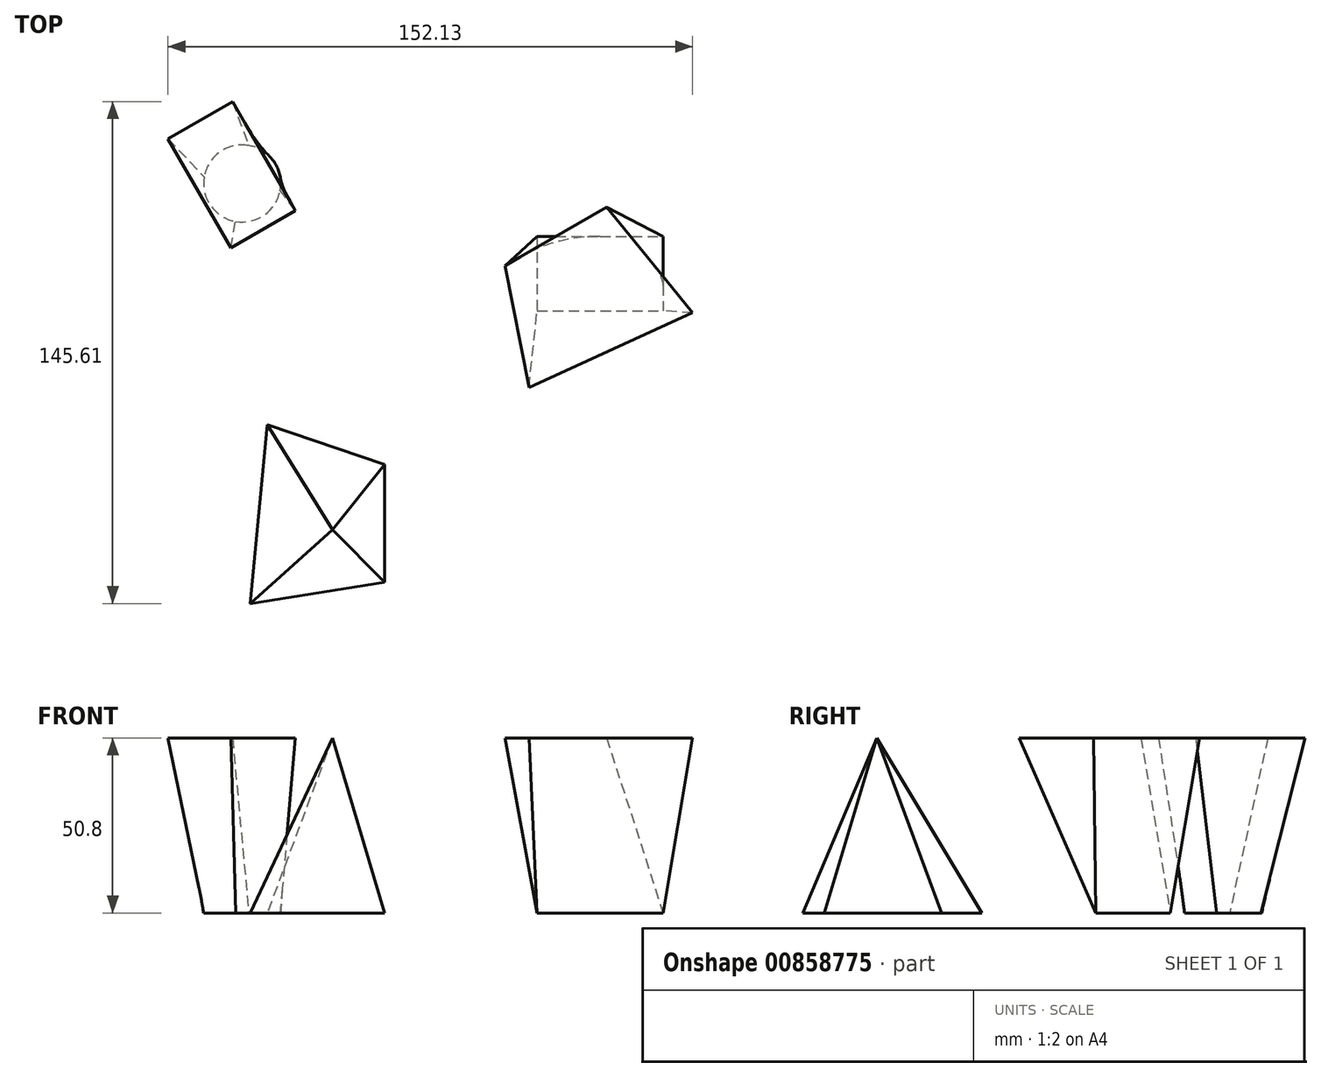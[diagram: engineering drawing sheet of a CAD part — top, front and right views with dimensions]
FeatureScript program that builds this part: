
annotation { "Feature Type Name" : "Feature", "Feature Type Description" : "" }
export const myFeature = defineFeature(function(context is Context, id is Id, definition is map)
    precondition{}
    {
        {
            var Q0;
            Q0=qCreatedBy(makeId("Top.planeOp"),FACE);
            var sketch = newSketch(context, id + "F0", { "sketchPlane" : qUnion([Q0])});
            skCircle(sketch, "E0", {"center": v(-62.28, 52.52) * mm, "radius": 11.18 * mm});
            skLineSegment(sketch, "E1.bottom", {"start": v(23.25, 37.16) * mm, "end": v(59.79, 37.16) * mm});
            skLineSegment(sketch, "E1.top", {"start": v(23.25, 15.57) * mm, "end": v(59.79, 15.57) * mm});
            skLineSegment(sketch, "E1.left", {"start": v(23.25, 37.16) * mm, "end": v(23.25, 15.57) * mm});
            skLineSegment(sketch, "E1.right", {"start": v(59.79, 37.16) * mm, "end": v(59.79, 15.57) * mm});
            skLineSegment(sketch, "E2", {"start": v(-55, -17.45) * mm, "end": v(-20.95, -29.08) * mm});
            skLineSegment(sketch, "E3", {"start": v(-20.95, -29.08) * mm, "end": v(-20.95, -63.13) * mm});
            skLineSegment(sketch, "E4", {"start": v(-20.95, -63.13) * mm, "end": v(-59.98, -69.35) * mm});
            skLineSegment(sketch, "E5", {"start": v(-59.98, -69.35) * mm, "end": v(-55, -17.45) * mm});
            skLineSegment(sketch, "E6", {"start": v(-82.91, 71.7) * mm, "end": v(-82.91, 30.26) * mm, "construction": true});
            skSolve(sketch);
        }
        {
            var Q0;
            Q0=qCreatedBy(makeId("Top.planeOp"),FACE);
            cPlane(context, id + "F1", {"entities" : qUnion([Q0]), "cplaneType" : CPlaneType.OFFSET, "offset" : 50.8 * mm, "width" : 152.4 * mm, "height" : 152.4 * mm});
        }
        {
            var Q0;
            Q0=qCreatedBy(id+"F1.planeOp",FACE);
            var sketch = newSketch(context, id + "F2", { "sketchPlane" : qUnion([Q0])});
            skCircle(sketch, "E7.0", {"center": v(-36.07, -47.94) * mm, "radius": 11.18 * mm});
            skLineSegment(sketch, "E7.1.0", {"start": v(-65.53, 33.82) * mm, "end": v(-46.83, 44.61) * mm});
            skLineSegment(sketch, "E7.1.1", {"start": v(-46.83, 44.61) * mm, "end": v(-65.1, 76.26) * mm});
            skLineSegment(sketch, "E7.1.2", {"start": v(-65.1, 76.26) * mm, "end": v(-83.8, 65.46) * mm});
            skLineSegment(sketch, "E7.1.3", {"start": v(-83.8, 65.46) * mm, "end": v(-65.53, 33.82) * mm});
            skLineSegment(sketch, "E7.2.0", {"start": v(20.9, -6.64) * mm, "end": v(68.33, 15) * mm});
            skLineSegment(sketch, "E7.2.1", {"start": v(68.33, 15) * mm, "end": v(43.42, 45.68) * mm});
            skLineSegment(sketch, "E7.2.2", {"start": v(43.42, 45.68) * mm, "end": v(13.94, 28.66) * mm});
            skLineSegment(sketch, "E7.2.3", {"start": v(13.94, 28.66) * mm, "end": v(20.9, -6.64) * mm});
            skSolve(sketch);
        }
        {
            var Q0;
            Q0=makeQuery(id+"F2.imprint","IMPRINT",FACE,{"disambiguationData":[TD([[makeQuery(id+"F2.imprint","IMPRINT",EDGE,{"derivedFrom":sQuery(id+"F2.wireOp",EDGE,"E7.2.0")}),1.0]])]});
            var Q1;
            Q1=makeQuery(id+"F0.imprint","IMPRINT",FACE,{"disambiguationData":[TD([[makeQuery(id+"F0.imprint","IMPRINT",EDGE,{"derivedFrom":sQuery(id+"F0.wireOp",EDGE,"E1.bottom")}),-1.0]])]});
            loft(context, id + "F3", {"sheetProfilesArray" : [{ "sheetProfileEntities" : qUnion([Q0]) }, { "sheetProfileEntities" : qUnion([Q1]) }]});
        }
        {
            var Q0;
            Q0=makeQuery(id+"F2.imprint","IMPRINT",FACE,{"disambiguationData":[TD([[makeQuery(id+"F2.imprint","IMPRINT",EDGE,{"derivedFrom":sQuery(id+"F2.wireOp",EDGE,"E7.1.0")}),1.0]])]});
            var Q1;
            Q1=makeQuery(id+"F0.imprint","IMPRINT",FACE,{"disambiguationData":[TD([[makeQuery(id+"F0.imprint","IMPRINT",EDGE,{"derivedFrom":sQuery(id+"F0.wireOp",EDGE,"E0")}),1.0]])]});
            loft(context, id + "F4", {"sheetProfilesArray" : [{ "sheetProfileEntities" : qUnion([Q0]) }, { "sheetProfileEntities" : qUnion([Q1]) }]});
        }
        {
            var Q0;
            Q0=sQuery(id+"F2.wireOp",VERTEX,"E7.0.center");
            var Q1;
            Q1=makeQuery(id+"F0.imprint","IMPRINT",FACE,{"disambiguationData":[TD([[makeQuery(id+"F0.imprint","IMPRINT",EDGE,{"derivedFrom":sQuery(id+"F0.wireOp",EDGE,"E2")}),-1.0]])]});
            loft(context, id + "F5", {"sheetProfilesArray" : [{ "sheetProfileEntities" : qUnion([Q0]) }, { "sheetProfileEntities" : qUnion([Q1]) }]});
        }
    });
